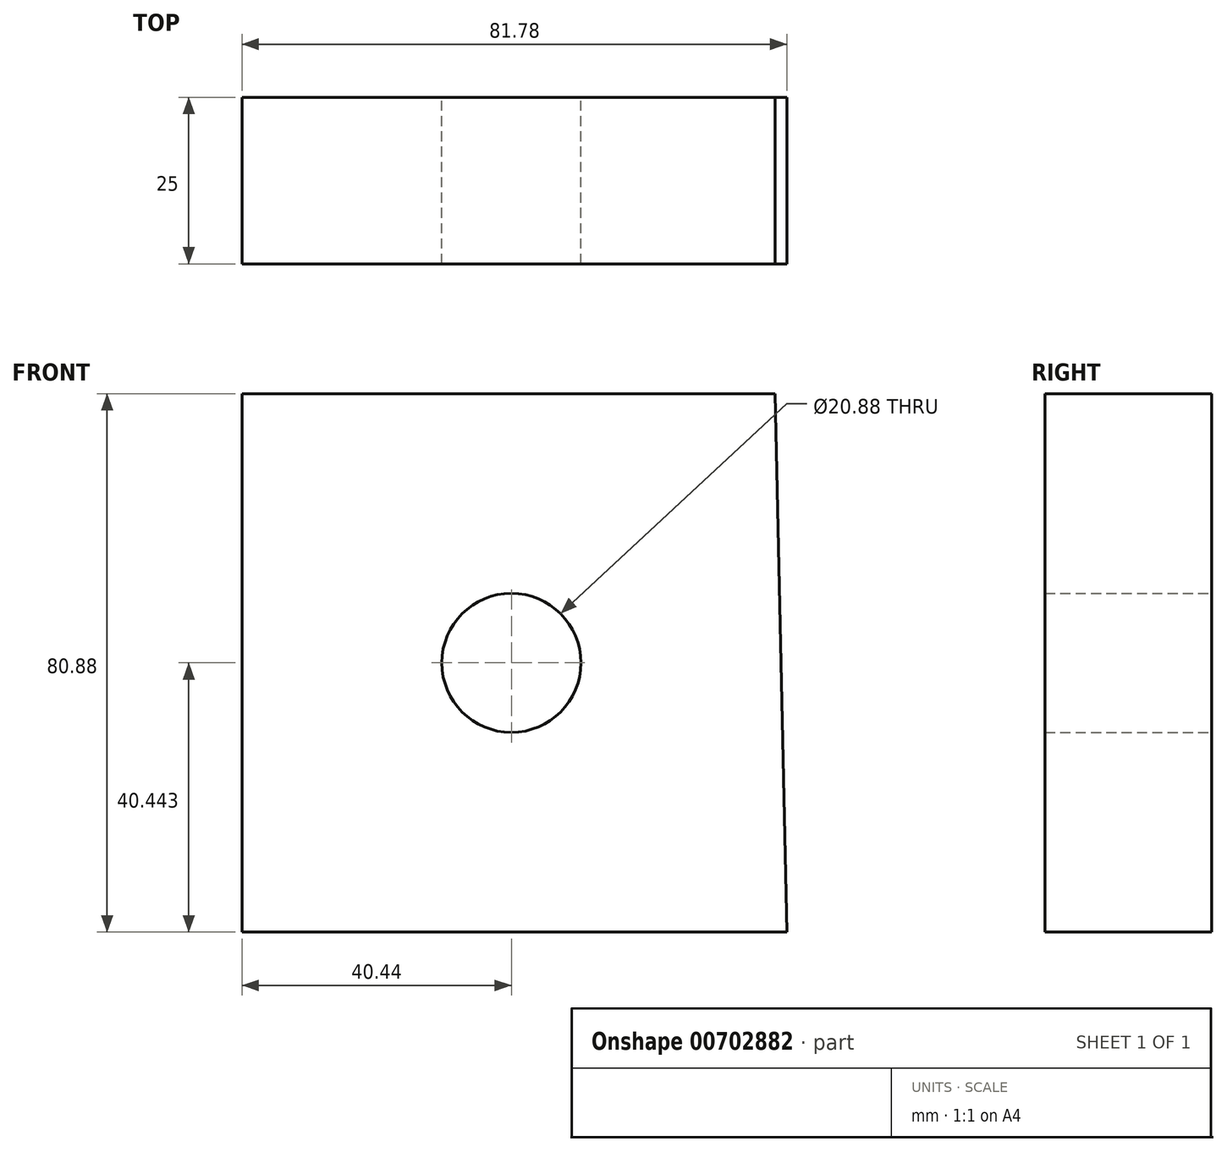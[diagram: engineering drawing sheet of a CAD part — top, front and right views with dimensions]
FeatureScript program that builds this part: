
annotation { "Feature Type Name" : "Feature", "Feature Type Description" : "" }
export const myFeature = defineFeature(function(context is Context, id is Id, definition is map)
    precondition{}
    {
        {
            var Q0;
            Q0=qCreatedBy(makeId("Front.planeOp"),FACE);
            var sketch = newSketch(context, id + "F0", { "sketchPlane" : qUnion([Q0])});
            skLineSegment(sketch, "E0", {"start": v(-40.44, 46.35) * mm, "end": v(39.56, 46.35) * mm});
            skLineSegment(sketch, "E1", {"start": v(-40.44, 46.35) * mm, "end": v(-40.44, -34.53) * mm});
            skLineSegment(sketch, "E2", {"start": v(-40.44, -34.53) * mm, "end": v(41.34, -34.53) * mm});
            skLineSegment(sketch, "E3", {"start": v(41.34, -34.53) * mm, "end": v(39.56, 46.35) * mm});
            skCircle(sketch, "E4", {"center": v(0, 5.91) * mm, "radius": 10.44 * mm});
            skSolve(sketch);
        }
        {
            var Q0;
            Q0 = qSketchRegion(id + "F0", true);
            extrude(context, id + "F1", {"entities" : qUnion([Q0]), "depth" : 25 * mm, "offsetDistance" : 25 * mm});
        }
    });
